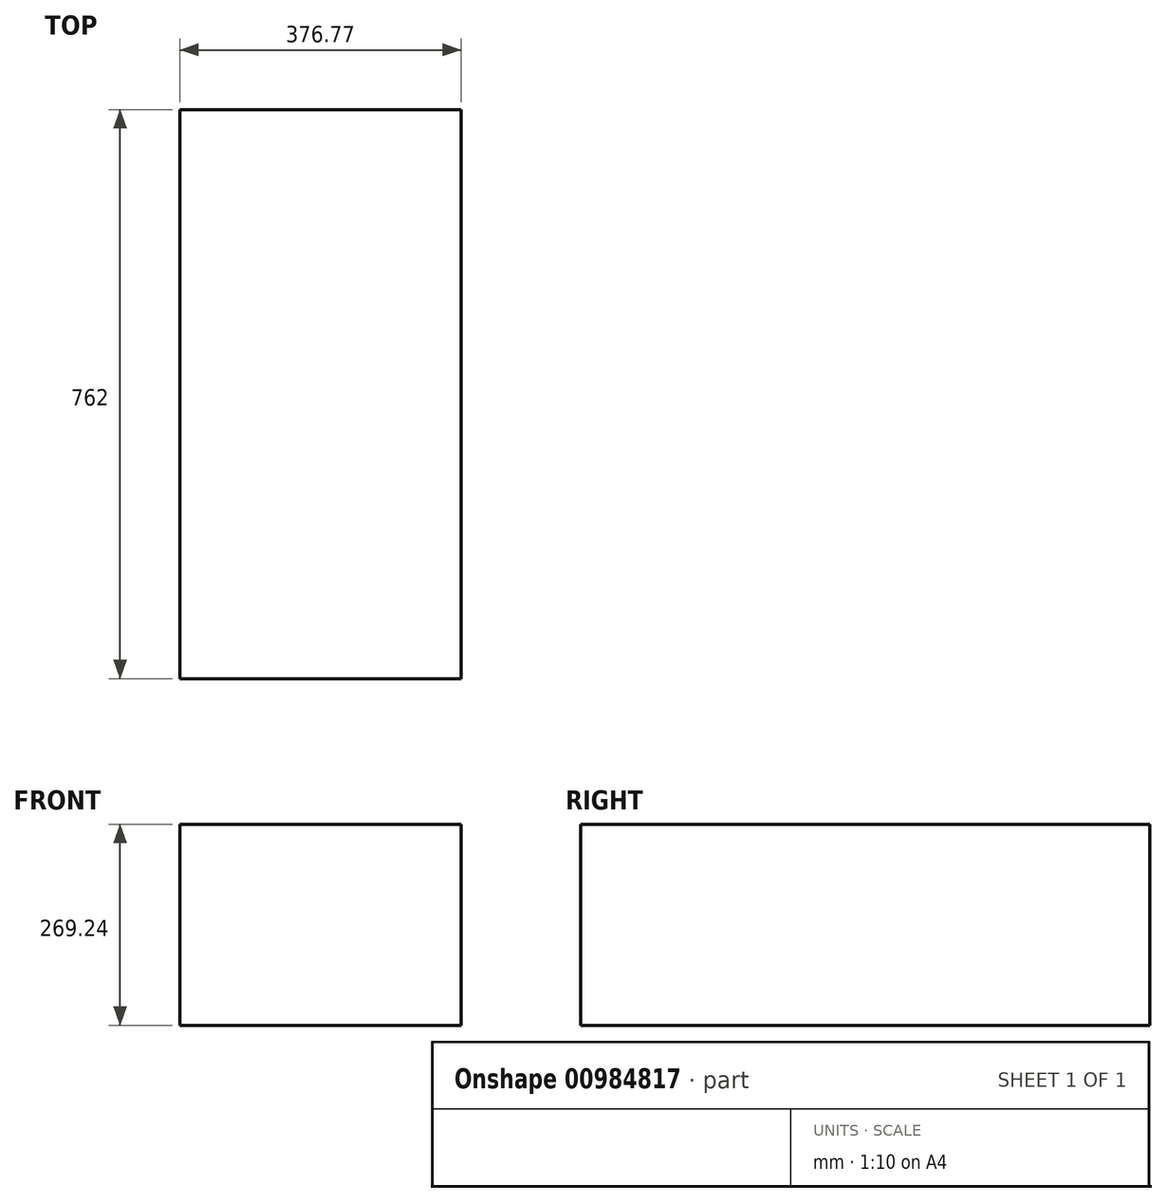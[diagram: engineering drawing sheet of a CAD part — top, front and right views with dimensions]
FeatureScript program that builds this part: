
annotation { "Feature Type Name" : "Feature", "Feature Type Description" : "" }
export const myFeature = defineFeature(function(context is Context, id is Id, definition is map)
    precondition{}
    {
        {
            var Q0;
            Q0=qCreatedBy(makeId("Front.planeOp"),FACE);
            var sketch = newSketch(context, id + "F0", { "sketchPlane" : qUnion([Q0])});
            skLineSegment(sketch, "E0.bottom", {"start": v(-175.87, 122.43) * mm, "end": v(200.9, 122.43) * mm});
            skLineSegment(sketch, "E0.top", {"start": v(-175.87, -146.8) * mm, "end": v(200.9, -146.8) * mm});
            skLineSegment(sketch, "E0.left", {"start": v(-175.87, 122.43) * mm, "end": v(-175.87, -146.8) * mm});
            skLineSegment(sketch, "E0.right", {"start": v(200.9, 122.43) * mm, "end": v(200.9, -146.8) * mm});
            skSolve(sketch);
        }
        {
            var Q0;
            Q0=makeQuery(id+"F0.imprint","IMPRINT",FACE,{"disambiguationData":[TD([[makeQuery(id+"F0.imprint","IMPRINT",EDGE,{"derivedFrom":sQuery(id+"F0.wireOp",EDGE,"E0.bottom")}),-1.0]])]});
            extrude(context, id + "F1", {"entities" : qUnion([Q0]), "endBound" : BoundingType.SYMMETRIC, "depth" : 762 * mm, "offsetDistance" : 25.4 * mm});
        }
    });
